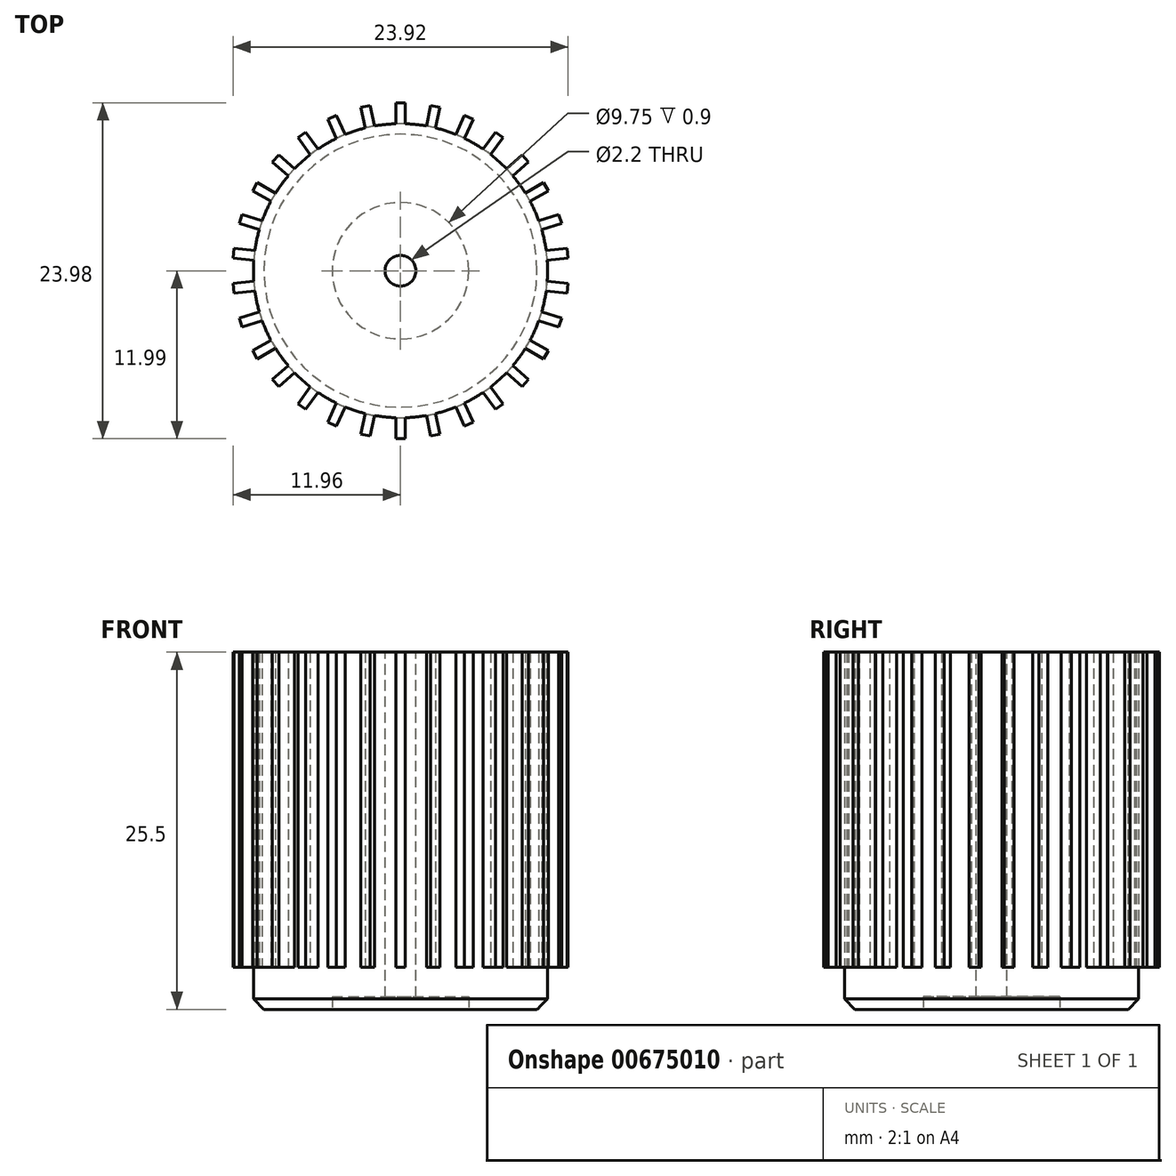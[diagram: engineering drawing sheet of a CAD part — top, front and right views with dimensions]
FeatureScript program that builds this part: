
annotation { "Feature Type Name" : "Feature", "Feature Type Description" : "" }
export const myFeature = defineFeature(function(context is Context, id is Id, definition is map)
    precondition{}
    {
        {
            assignVariable(context, id + "F0", {"name" : "Faktor", "anyValue" : 1.5});
        }
        {
            var Q0;
            Q0=qCreatedBy(makeId("Top.planeOp"),FACE);
            var sketch = newSketch(context, id + "F1", { "sketchPlane" : qUnion([Q0])});
            skCircle(sketch, "E0", {"center": v(0, 0) * mm, "radius": 10.5 * mm});
            skSolve(sketch);
        }
        {
            var Q0;
            Q0=qSketchRegion(id+"F1",true);
            extrude(context, id + "F2", {"entities" : qUnion([Q0]), "depth" : getVariable(context, 'Faktor') * 15 * mm, "offsetDistance" : 25 * mm});
        }
        {
            var Q0;
            Q0=qCreatedBy(makeId("Top.planeOp"),FACE);
            var sketch = newSketch(context, id + "F3", { "sketchPlane" : qUnion([Q0])});
            skArc(sketch, "E1.0", {"start": v(0.34, 10.5) * mm, "mid": v(0, 10.5) * mm, "end": v(-0.34, 10.5) * mm});
            skLineSegment(sketch, "E2", {"start": v(-0.34, 10.5) * mm, "end": v(-0.34, 12) * mm});
            skLineSegment(sketch, "E3", {"start": v(-0.34, 12) * mm, "end": v(0.34, 12) * mm});
            skLineSegment(sketch, "E4", {"start": v(0.34, 12) * mm, "end": v(0.34, 10.5) * mm});
            skSolve(sketch);
        }
        {
            var Q0;
            Q0=qSketchRegion(id+"F3",true);
            extrude(context, id + "F4", {"entities" : qUnion([Q0]), "depth" : getVariable(context, 'Faktor') * 15 * mm, "offsetDistance" : 25 * mm});
        }
        {
            var Q0;
            Q0=makeQuery(id+"F4.opExtrude","SWEPT_BODY",BODY,{"disambiguationData":[OSD([sQuery(id+"F3.wireOp",EDGE,"E1.0"),sQuery(id+"F3.wireOp",EDGE,"E2"),sQuery(id+"F3.wireOp",EDGE,"E3"),sQuery(id+"F3.wireOp",EDGE,"E4")])]});
            var Q1;
            Q1=makeQuery(id+"F2.opExtrude","CAP_EDGE",EDGE,{"disambiguationData":[OSD([sQuery(id+"F1.wireOp",EDGE,"E0")])],"isStart":false});
            circularPattern(context, id + "F5", {"entities" : qUnion([Q0]), "axis" : qUnion([Q1]), "angle" : 360 * degree, "instanceCount" : 30, "equalSpace" : true});
        }
        {
            var Q0;
            Q0=makeQuery(id+"F5.opPattern","COPY",BODY,{"derivedFrom":makeQuery(id+"F4.opExtrude","SWEPT_BODY",BODY,{"disambiguationData":[OSD([sQuery(id+"F3.wireOp",EDGE,"E1.0"),sQuery(id+"F3.wireOp",EDGE,"E2"),sQuery(id+"F3.wireOp",EDGE,"E3"),sQuery(id+"F3.wireOp",EDGE,"E4")])]}),"instanceName":"4"});
            var Q1;
            Q1=makeQuery(id+"F5.opPattern","COPY",BODY,{"derivedFrom":makeQuery(id+"F4.opExtrude","SWEPT_BODY",BODY,{"disambiguationData":[OSD([sQuery(id+"F3.wireOp",EDGE,"E1.0"),sQuery(id+"F3.wireOp",EDGE,"E2"),sQuery(id+"F3.wireOp",EDGE,"E3"),sQuery(id+"F3.wireOp",EDGE,"E4")])]}),"instanceName":"2"});
            var Q2;
            Q2=makeQuery(id+"F5.opPattern","COPY",BODY,{"derivedFrom":makeQuery(id+"F4.opExtrude","SWEPT_BODY",BODY,{"disambiguationData":[OSD([sQuery(id+"F3.wireOp",EDGE,"E1.0"),sQuery(id+"F3.wireOp",EDGE,"E2"),sQuery(id+"F3.wireOp",EDGE,"E3"),sQuery(id+"F3.wireOp",EDGE,"E4")])]}),"instanceName":"11"});
            var Q3;
            Q3=makeQuery(id+"F5.opPattern","COPY",BODY,{"derivedFrom":makeQuery(id+"F4.opExtrude","SWEPT_BODY",BODY,{"disambiguationData":[OSD([sQuery(id+"F3.wireOp",EDGE,"E1.0"),sQuery(id+"F3.wireOp",EDGE,"E2"),sQuery(id+"F3.wireOp",EDGE,"E3"),sQuery(id+"F3.wireOp",EDGE,"E4")])]}),"instanceName":"1"});
            var Q4;
            Q4=makeQuery(id+"F5.opPattern","COPY",BODY,{"derivedFrom":makeQuery(id+"F4.opExtrude","SWEPT_BODY",BODY,{"disambiguationData":[OSD([sQuery(id+"F3.wireOp",EDGE,"E1.0"),sQuery(id+"F3.wireOp",EDGE,"E2"),sQuery(id+"F3.wireOp",EDGE,"E3"),sQuery(id+"F3.wireOp",EDGE,"E4")])]}),"instanceName":"3"});
            var Q5;
            Q5=makeQuery(id+"F5.opPattern","COPY",BODY,{"derivedFrom":makeQuery(id+"F4.opExtrude","SWEPT_BODY",BODY,{"disambiguationData":[OSD([sQuery(id+"F3.wireOp",EDGE,"E1.0"),sQuery(id+"F3.wireOp",EDGE,"E2"),sQuery(id+"F3.wireOp",EDGE,"E3"),sQuery(id+"F3.wireOp",EDGE,"E4")])]}),"instanceName":"6"});
            var Q6;
            Q6=makeQuery(id+"F4.opExtrude","SWEPT_BODY",BODY,{"disambiguationData":[OSD([sQuery(id+"F3.wireOp",EDGE,"E1.0"),sQuery(id+"F3.wireOp",EDGE,"E2"),sQuery(id+"F3.wireOp",EDGE,"E3"),sQuery(id+"F3.wireOp",EDGE,"E4")])]});
            var Q7;
            Q7=makeQuery(id+"F5.opPattern","COPY",BODY,{"derivedFrom":makeQuery(id+"F4.opExtrude","SWEPT_BODY",BODY,{"disambiguationData":[OSD([sQuery(id+"F3.wireOp",EDGE,"E1.0"),sQuery(id+"F3.wireOp",EDGE,"E2"),sQuery(id+"F3.wireOp",EDGE,"E3"),sQuery(id+"F3.wireOp",EDGE,"E4")])]}),"instanceName":"13"});
            var Q8;
            Q8=makeQuery(id+"F5.opPattern","COPY",BODY,{"derivedFrom":makeQuery(id+"F4.opExtrude","SWEPT_BODY",BODY,{"disambiguationData":[OSD([sQuery(id+"F3.wireOp",EDGE,"E1.0"),sQuery(id+"F3.wireOp",EDGE,"E2"),sQuery(id+"F3.wireOp",EDGE,"E3"),sQuery(id+"F3.wireOp",EDGE,"E4")])]}),"instanceName":"8"});
            var Q9;
            Q9=makeQuery(id+"F5.opPattern","COPY",BODY,{"derivedFrom":makeQuery(id+"F4.opExtrude","SWEPT_BODY",BODY,{"disambiguationData":[OSD([sQuery(id+"F3.wireOp",EDGE,"E1.0"),sQuery(id+"F3.wireOp",EDGE,"E2"),sQuery(id+"F3.wireOp",EDGE,"E3"),sQuery(id+"F3.wireOp",EDGE,"E4")])]}),"instanceName":"7"});
            var Q10;
            Q10=makeQuery(id+"F5.opPattern","COPY",BODY,{"derivedFrom":makeQuery(id+"F4.opExtrude","SWEPT_BODY",BODY,{"disambiguationData":[OSD([sQuery(id+"F3.wireOp",EDGE,"E1.0"),sQuery(id+"F3.wireOp",EDGE,"E2"),sQuery(id+"F3.wireOp",EDGE,"E3"),sQuery(id+"F3.wireOp",EDGE,"E4")])]}),"instanceName":"5"});
            var Q11;
            Q11=makeQuery(id+"F5.opPattern","COPY",BODY,{"derivedFrom":makeQuery(id+"F4.opExtrude","SWEPT_BODY",BODY,{"disambiguationData":[OSD([sQuery(id+"F3.wireOp",EDGE,"E1.0"),sQuery(id+"F3.wireOp",EDGE,"E2"),sQuery(id+"F3.wireOp",EDGE,"E3"),sQuery(id+"F3.wireOp",EDGE,"E4")])]}),"instanceName":"9"});
            var Q12;
            Q12=makeQuery(id+"F2.opExtrude","SWEPT_BODY",BODY,{"disambiguationData":[OSD([sQuery(id+"F1.wireOp",EDGE,"E0")])]});
            var Q13;
            Q13=makeQuery(id+"F5.opPattern","COPY",BODY,{"derivedFrom":makeQuery(id+"F4.opExtrude","SWEPT_BODY",BODY,{"disambiguationData":[OSD([sQuery(id+"F3.wireOp",EDGE,"E1.0"),sQuery(id+"F3.wireOp",EDGE,"E2"),sQuery(id+"F3.wireOp",EDGE,"E3"),sQuery(id+"F3.wireOp",EDGE,"E4")])]}),"instanceName":"10"});
            var Q14;
            Q14=makeQuery(id+"F5.opPattern","COPY",BODY,{"derivedFrom":makeQuery(id+"F4.opExtrude","SWEPT_BODY",BODY,{"disambiguationData":[OSD([sQuery(id+"F3.wireOp",EDGE,"E1.0"),sQuery(id+"F3.wireOp",EDGE,"E2"),sQuery(id+"F3.wireOp",EDGE,"E3"),sQuery(id+"F3.wireOp",EDGE,"E4")])]}),"instanceName":"14"});
            var Q15;
            Q15=makeQuery(id+"F5.opPattern","COPY",BODY,{"derivedFrom":makeQuery(id+"F4.opExtrude","SWEPT_BODY",BODY,{"disambiguationData":[OSD([sQuery(id+"F3.wireOp",EDGE,"E1.0"),sQuery(id+"F3.wireOp",EDGE,"E2"),sQuery(id+"F3.wireOp",EDGE,"E3"),sQuery(id+"F3.wireOp",EDGE,"E4")])]}),"instanceName":"12"});
            var Q16;
            Q16=makeQuery(id+"F5.opPattern","COPY",BODY,{"derivedFrom":makeQuery(id+"F4.opExtrude","SWEPT_BODY",BODY,{"disambiguationData":[OSD([sQuery(id+"F3.wireOp",EDGE,"E1.0"),sQuery(id+"F3.wireOp",EDGE,"E2"),sQuery(id+"F3.wireOp",EDGE,"E3"),sQuery(id+"F3.wireOp",EDGE,"E4")])]}),"instanceName":"18"});
            var Q17;
            Q17=makeQuery(id+"F5.opPattern","COPY",BODY,{"derivedFrom":makeQuery(id+"F4.opExtrude","SWEPT_BODY",BODY,{"disambiguationData":[OSD([sQuery(id+"F3.wireOp",EDGE,"E1.0"),sQuery(id+"F3.wireOp",EDGE,"E2"),sQuery(id+"F3.wireOp",EDGE,"E3"),sQuery(id+"F3.wireOp",EDGE,"E4")])]}),"instanceName":"17"});
            var Q18;
            Q18=makeQuery(id+"F5.opPattern","COPY",BODY,{"derivedFrom":makeQuery(id+"F4.opExtrude","SWEPT_BODY",BODY,{"disambiguationData":[OSD([sQuery(id+"F3.wireOp",EDGE,"E1.0"),sQuery(id+"F3.wireOp",EDGE,"E2"),sQuery(id+"F3.wireOp",EDGE,"E3"),sQuery(id+"F3.wireOp",EDGE,"E4")])]}),"instanceName":"16"});
            var Q19;
            Q19=makeQuery(id+"F5.opPattern","COPY",BODY,{"derivedFrom":makeQuery(id+"F4.opExtrude","SWEPT_BODY",BODY,{"disambiguationData":[OSD([sQuery(id+"F3.wireOp",EDGE,"E1.0"),sQuery(id+"F3.wireOp",EDGE,"E2"),sQuery(id+"F3.wireOp",EDGE,"E3"),sQuery(id+"F3.wireOp",EDGE,"E4")])]}),"instanceName":"15"});
            var Q20;
            Q20=makeQuery(id+"F5.opPattern","COPY",BODY,{"derivedFrom":makeQuery(id+"F4.opExtrude","SWEPT_BODY",BODY,{"disambiguationData":[OSD([sQuery(id+"F3.wireOp",EDGE,"E1.0"),sQuery(id+"F3.wireOp",EDGE,"E2"),sQuery(id+"F3.wireOp",EDGE,"E3"),sQuery(id+"F3.wireOp",EDGE,"E4")])]}),"instanceName":"19"});
            var Q21;
            Q21=makeQuery(id+"F5.opPattern","COPY",BODY,{"derivedFrom":makeQuery(id+"F4.opExtrude","SWEPT_BODY",BODY,{"disambiguationData":[OSD([sQuery(id+"F3.wireOp",EDGE,"E1.0"),sQuery(id+"F3.wireOp",EDGE,"E2"),sQuery(id+"F3.wireOp",EDGE,"E3"),sQuery(id+"F3.wireOp",EDGE,"E4")])]}),"instanceName":"20"});
            var Q22;
            Q22=makeQuery(id+"F5.opPattern","COPY",BODY,{"derivedFrom":makeQuery(id+"F4.opExtrude","SWEPT_BODY",BODY,{"disambiguationData":[OSD([sQuery(id+"F3.wireOp",EDGE,"E1.0"),sQuery(id+"F3.wireOp",EDGE,"E2"),sQuery(id+"F3.wireOp",EDGE,"E3"),sQuery(id+"F3.wireOp",EDGE,"E4")])]}),"instanceName":"21"});
            var Q23;
            Q23=makeQuery(id+"F5.opPattern","COPY",BODY,{"derivedFrom":makeQuery(id+"F4.opExtrude","SWEPT_BODY",BODY,{"disambiguationData":[OSD([sQuery(id+"F3.wireOp",EDGE,"E1.0"),sQuery(id+"F3.wireOp",EDGE,"E2"),sQuery(id+"F3.wireOp",EDGE,"E3"),sQuery(id+"F3.wireOp",EDGE,"E4")])]}),"instanceName":"22"});
            var Q24;
            Q24=makeQuery(id+"F5.opPattern","COPY",BODY,{"derivedFrom":makeQuery(id+"F4.opExtrude","SWEPT_BODY",BODY,{"disambiguationData":[OSD([sQuery(id+"F3.wireOp",EDGE,"E1.0"),sQuery(id+"F3.wireOp",EDGE,"E2"),sQuery(id+"F3.wireOp",EDGE,"E3"),sQuery(id+"F3.wireOp",EDGE,"E4")])]}),"instanceName":"23"});
            var Q25;
            Q25=makeQuery(id+"F5.opPattern","COPY",BODY,{"derivedFrom":makeQuery(id+"F4.opExtrude","SWEPT_BODY",BODY,{"disambiguationData":[OSD([sQuery(id+"F3.wireOp",EDGE,"E1.0"),sQuery(id+"F3.wireOp",EDGE,"E2"),sQuery(id+"F3.wireOp",EDGE,"E3"),sQuery(id+"F3.wireOp",EDGE,"E4")])]}),"instanceName":"24"});
            var Q26;
            Q26=makeQuery(id+"F5.opPattern","COPY",BODY,{"derivedFrom":makeQuery(id+"F4.opExtrude","SWEPT_BODY",BODY,{"disambiguationData":[OSD([sQuery(id+"F3.wireOp",EDGE,"E1.0"),sQuery(id+"F3.wireOp",EDGE,"E2"),sQuery(id+"F3.wireOp",EDGE,"E3"),sQuery(id+"F3.wireOp",EDGE,"E4")])]}),"instanceName":"25"});
            var Q27;
            Q27=makeQuery(id+"F5.opPattern","COPY",BODY,{"derivedFrom":makeQuery(id+"F4.opExtrude","SWEPT_BODY",BODY,{"disambiguationData":[OSD([sQuery(id+"F3.wireOp",EDGE,"E1.0"),sQuery(id+"F3.wireOp",EDGE,"E2"),sQuery(id+"F3.wireOp",EDGE,"E3"),sQuery(id+"F3.wireOp",EDGE,"E4")])]}),"instanceName":"26"});
            var Q28;
            Q28=makeQuery(id+"F5.opPattern","COPY",BODY,{"derivedFrom":makeQuery(id+"F4.opExtrude","SWEPT_BODY",BODY,{"disambiguationData":[OSD([sQuery(id+"F3.wireOp",EDGE,"E1.0"),sQuery(id+"F3.wireOp",EDGE,"E2"),sQuery(id+"F3.wireOp",EDGE,"E3"),sQuery(id+"F3.wireOp",EDGE,"E4")])]}),"instanceName":"27"});
            var Q29;
            Q29=makeQuery(id+"F5.opPattern","COPY",BODY,{"derivedFrom":makeQuery(id+"F4.opExtrude","SWEPT_BODY",BODY,{"disambiguationData":[OSD([sQuery(id+"F3.wireOp",EDGE,"E1.0"),sQuery(id+"F3.wireOp",EDGE,"E2"),sQuery(id+"F3.wireOp",EDGE,"E3"),sQuery(id+"F3.wireOp",EDGE,"E4")])]}),"instanceName":"28"});
            var Q30;
            Q30=makeQuery(id+"F5.opPattern","COPY",BODY,{"derivedFrom":makeQuery(id+"F4.opExtrude","SWEPT_BODY",BODY,{"disambiguationData":[OSD([sQuery(id+"F3.wireOp",EDGE,"E1.0"),sQuery(id+"F3.wireOp",EDGE,"E2"),sQuery(id+"F3.wireOp",EDGE,"E3"),sQuery(id+"F3.wireOp",EDGE,"E4")])]}),"instanceName":"29"});
            booleanBodies(context, id + "F6", {"operationType" : BooleanOperationType.UNION, "tools" : qUnion([Q0, Q1, Q2, Q3, Q4, Q5, Q6, Q7, Q8, Q9, Q10, Q11, Q12, Q13, Q14, Q15, Q16, Q17, Q18, Q19, Q20, Q21, Q22, Q23, Q24, Q25, Q26, Q27, Q28, Q29, Q30])});
        }
        {
            var Q0;
            Q0=qCreatedBy(makeId("Top.planeOp"),FACE);
            var sketch = newSketch(context, id + "F7", { "sketchPlane" : qUnion([Q0])});
            skCircle(sketch, "E5", {"center": v(0, 0) * mm, "radius": 10.5 * mm});
            skSolve(sketch);
        }
        {
            var Q0;
            Q0=qSketchRegion(id+"F7",true);
            extrude(context, id + "F8", {"entities" : qUnion([Q0]), "operationType" : NewBodyOperationType.ADD, "oppositeDirection" : true, "depth" : getVariable(context, 'Faktor') * 2 * mm, "offsetDistance" : 25 * mm});
        }
        {
            var Q0;
            Q0=makeQuery(id+"F8.opExtrude","CAP_EDGE",EDGE,{"disambiguationData":[OSD([sQuery(id+"F7.wireOp",EDGE,"E5")])],"isStart":false});
            chamfer(context, id + "F9", {"entities" : qUnion([Q0]), "width" : getVariable(context, 'Faktor') * 0.5 * mm, "tangentPropagation" : true});
        }
        {
            var Q0;
            Q0=makeQuery(id+"F8.opExtrude","CAP_FACE",FACE,{"disambiguationData":[OSD([sQuery(id+"F7.wireOp",EDGE,"E5")])],"isStart":false});
            var sketch = newSketch(context, id + "F10", { "sketchPlane" : qUnion([Q0])});
            skCircle(sketch, "E6", {"center": v(0, 0) * mm, "radius": 4.88 * mm});
            skSolve(sketch);
        }
        {
            var Q0;
            Q0=qSketchRegion(id+"F10",true);
            extrude(context, id + "F11", {"entities" : qUnion([Q0]), "operationType" : NewBodyOperationType.REMOVE, "oppositeDirection" : true, "depth" : getVariable(context, 'Faktor') * 0.6 * mm, "offsetDistance" : 25 * mm});
        }
        {
            var Q0;
            Q0=makeQuery(id+"F11.boolean.opBoolean","COPY",FACE,{"derivedFrom":makeQuery(id+"F11.opExtrude","CAP_FACE",FACE,{"disambiguationData":[OSD([sQuery(id+"F10.wireOp",EDGE,"E6")])],"isStart":false})});
            var sketch = newSketch(context, id + "F12", { "sketchPlane" : qUnion([Q0])});
            skCircle(sketch, "E7", {"center": v(0, 0) * mm, "radius": 1 * mm});
            skSolve(sketch);
        }
        {
            var Q0;
            {var subQ0=makeQuery(id+"F4.opExtrude","CAP_FACE",FACE,{"disambiguationData":[OSD([sQuery(id+"F3.wireOp",EDGE,"E1.0"),sQuery(id+"F3.wireOp",EDGE,"E2"),sQuery(id+"F3.wireOp",EDGE,"E3"),sQuery(id+"F3.wireOp",EDGE,"E4")])],"isStart":false});Q0=makeQuery(id+"F6.opBoolean","MERGE",FACE,{"derivedFrom":[makeQuery(id+"F2.opExtrude","CAP_FACE",FACE,{"disambiguationData":[OSD([sQuery(id+"F1.wireOp",EDGE,"E0")])],"isStart":false}),subQ0,makeQuery(id+"F5.opPattern","COPY",FACE,{"derivedFrom":subQ0,"instanceName":"1"}),makeQuery(id+"F5.opPattern","COPY",FACE,{"derivedFrom":subQ0,"instanceName":"2"}),makeQuery(id+"F5.opPattern","COPY",FACE,{"derivedFrom":subQ0,"instanceName":"3"}),makeQuery(id+"F5.opPattern","COPY",FACE,{"derivedFrom":subQ0,"instanceName":"4"}),makeQuery(id+"F5.opPattern","COPY",FACE,{"derivedFrom":subQ0,"instanceName":"5"}),makeQuery(id+"F5.opPattern","COPY",FACE,{"derivedFrom":subQ0,"instanceName":"6"}),makeQuery(id+"F5.opPattern","COPY",FACE,{"derivedFrom":subQ0,"instanceName":"7"}),makeQuery(id+"F5.opPattern","COPY",FACE,{"derivedFrom":subQ0,"instanceName":"8"}),makeQuery(id+"F5.opPattern","COPY",FACE,{"derivedFrom":subQ0,"instanceName":"9"}),makeQuery(id+"F5.opPattern","COPY",FACE,{"derivedFrom":subQ0,"instanceName":"10"}),makeQuery(id+"F5.opPattern","COPY",FACE,{"derivedFrom":subQ0,"instanceName":"11"}),makeQuery(id+"F5.opPattern","COPY",FACE,{"derivedFrom":subQ0,"instanceName":"12"}),makeQuery(id+"F5.opPattern","COPY",FACE,{"derivedFrom":subQ0,"instanceName":"13"}),makeQuery(id+"F5.opPattern","COPY",FACE,{"derivedFrom":subQ0,"instanceName":"14"}),makeQuery(id+"F5.opPattern","COPY",FACE,{"derivedFrom":subQ0,"instanceName":"15"}),makeQuery(id+"F5.opPattern","COPY",FACE,{"derivedFrom":subQ0,"instanceName":"16"}),makeQuery(id+"F5.opPattern","COPY",FACE,{"derivedFrom":subQ0,"instanceName":"17"}),makeQuery(id+"F5.opPattern","COPY",FACE,{"derivedFrom":subQ0,"instanceName":"18"}),makeQuery(id+"F5.opPattern","COPY",FACE,{"derivedFrom":subQ0,"instanceName":"19"}),makeQuery(id+"F5.opPattern","COPY",FACE,{"derivedFrom":subQ0,"instanceName":"20"}),makeQuery(id+"F5.opPattern","COPY",FACE,{"derivedFrom":subQ0,"instanceName":"21"}),makeQuery(id+"F5.opPattern","COPY",FACE,{"derivedFrom":subQ0,"instanceName":"22"}),makeQuery(id+"F5.opPattern","COPY",FACE,{"derivedFrom":subQ0,"instanceName":"23"}),makeQuery(id+"F5.opPattern","COPY",FACE,{"derivedFrom":subQ0,"instanceName":"24"}),makeQuery(id+"F5.opPattern","COPY",FACE,{"derivedFrom":subQ0,"instanceName":"25"}),makeQuery(id+"F5.opPattern","COPY",FACE,{"derivedFrom":subQ0,"instanceName":"26"}),makeQuery(id+"F5.opPattern","COPY",FACE,{"derivedFrom":subQ0,"instanceName":"27"}),makeQuery(id+"F5.opPattern","COPY",FACE,{"derivedFrom":subQ0,"instanceName":"28"}),makeQuery(id+"F5.opPattern","COPY",FACE,{"derivedFrom":subQ0,"instanceName":"29"})]});}
            var sketch = newSketch(context, id + "F13", { "sketchPlane" : qUnion([Q0])});
            skCircle(sketch, "E8", {"center": v(0, 0) * mm, "radius": 1.1 * mm});
            skSolve(sketch);
        }
        {
            var Q0;
            Q0=qSketchRegion(id+"F13",true);
            extrude(context, id + "F14", {"entities" : qUnion([Q0]), "operationType" : NewBodyOperationType.REMOVE, "endBound" : BoundingType.SYMMETRIC, "oppositeDirection" : true, "depth" : getVariable(context, 'Faktor') * 50 * mm, "offsetDistance" : 25 * mm});
        }
    });
